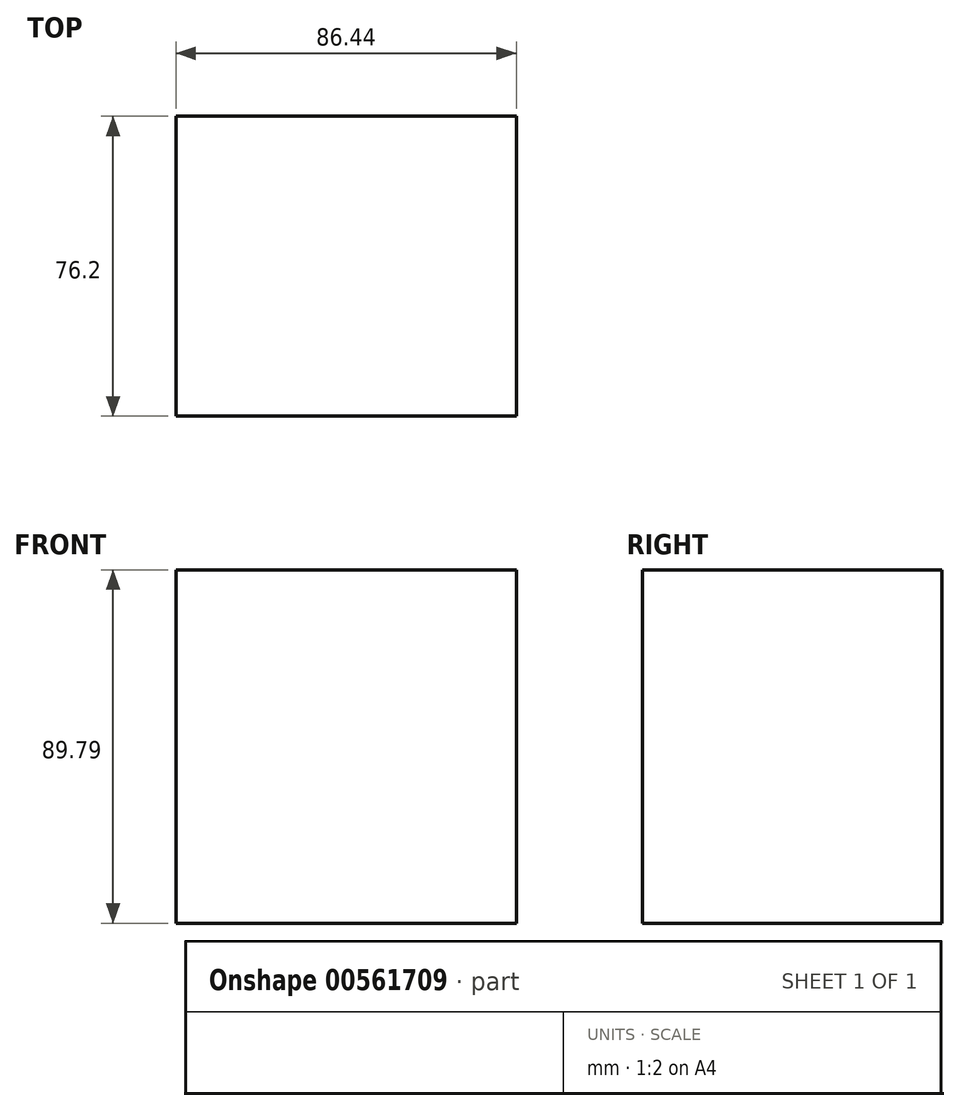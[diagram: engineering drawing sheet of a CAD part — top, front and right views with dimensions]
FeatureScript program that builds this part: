
annotation { "Feature Type Name" : "Feature", "Feature Type Description" : "" }
export const myFeature = defineFeature(function(context is Context, id is Id, definition is map)
    precondition{}
    {
        {
            var Q0;
            Q0=qCreatedBy(makeId("Front.planeOp"),FACE);
            var sketch = newSketch(context, id + "F0", { "sketchPlane" : qUnion([Q0])});
            skLineSegment(sketch, "E0.bottom", {"start": v(0, 0) * mm, "end": v(-86.44, 0) * mm});
            skLineSegment(sketch, "E0.top", {"start": v(0, 89.8) * mm, "end": v(-86.44, 89.8) * mm});
            skLineSegment(sketch, "E0.left", {"start": v(0, 0) * mm, "end": v(0, 89.8) * mm});
            skLineSegment(sketch, "E0.right", {"start": v(-86.44, 0) * mm, "end": v(-86.44, 89.8) * mm});
            skSolve(sketch);
        }
        {
            var Q0;
            Q0 = qSketchRegion(id + "F0", true);
            extrude(context, id + "F1", {"entities" : qUnion([Q0]), "oppositeDirection" : true, "depth" : 76.2 * mm, "offsetDistance" : 25.4 * mm});
        }
    });
